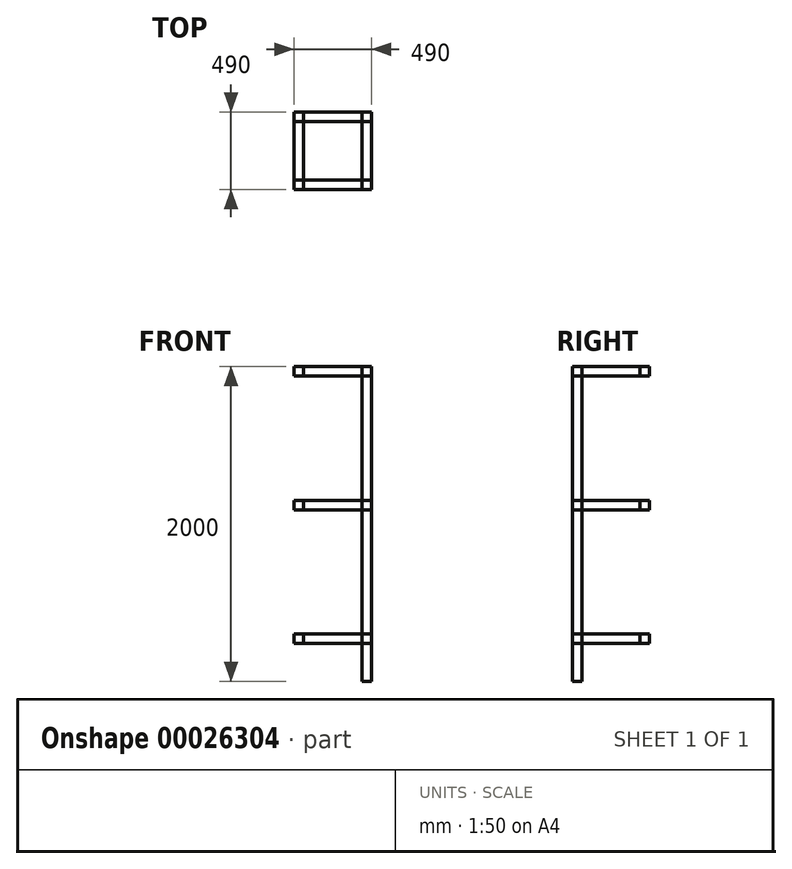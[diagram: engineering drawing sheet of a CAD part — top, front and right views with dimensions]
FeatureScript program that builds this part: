
annotation { "Feature Type Name" : "Feature", "Feature Type Description" : "" }
export const myFeature = defineFeature(function(context is Context, id is Id, definition is map)
    precondition{}
    {
        {
            var Q0;
            Q0=qCreatedBy(makeId("Top.planeOp"),FACE);
            var sketch = newSketch(context, id + "F0", { "sketchPlane" : qUnion([Q0])});
            skLineSegment(sketch, "E0.bottom", {"start": v(0, 0) * mm, "end": v(490, 0) * mm});
            skLineSegment(sketch, "E0.top", {"start": v(0, 490) * mm, "end": v(490, 490) * mm});
            skLineSegment(sketch, "E0.left", {"start": v(0, 0) * mm, "end": v(0, 490) * mm});
            skLineSegment(sketch, "E0.right", {"start": v(490, 0) * mm, "end": v(490, 490) * mm});
            skLineSegment(sketch, "E1.bottom", {"start": v(0, 0) * mm, "end": v(60, 0) * mm});
            skLineSegment(sketch, "E1.top", {"start": v(0, 60) * mm, "end": v(60, 60) * mm});
            skLineSegment(sketch, "E1.left", {"start": v(0, 0) * mm, "end": v(0, 60) * mm});
            skLineSegment(sketch, "E1.right", {"start": v(60, 0) * mm, "end": v(60, 60) * mm});
            skLineSegment(sketch, "E2.0.1.0", {"start": v(0, 490) * mm, "end": v(60, 490) * mm});
            skLineSegment(sketch, "E2.0.1.1", {"start": v(0, 430) * mm, "end": v(0, 490) * mm});
            skLineSegment(sketch, "E2.0.1.2", {"start": v(0, 430) * mm, "end": v(60, 430) * mm});
            skLineSegment(sketch, "E2.0.1.3", {"start": v(60, 430) * mm, "end": v(60, 490) * mm});
            skLineSegment(sketch, "E2.1.0.0", {"start": v(430, 60) * mm, "end": v(490, 60) * mm});
            skLineSegment(sketch, "E2.1.0.1", {"start": v(430, 0) * mm, "end": v(430, 60) * mm});
            skLineSegment(sketch, "E2.1.0.2", {"start": v(430, 0) * mm, "end": v(490, 0) * mm});
            skLineSegment(sketch, "E2.1.0.3", {"start": v(490, 0) * mm, "end": v(490, 60) * mm});
            skLineSegment(sketch, "E2.1.1.0", {"start": v(430, 490) * mm, "end": v(490, 490) * mm});
            skLineSegment(sketch, "E2.1.1.1", {"start": v(430, 430) * mm, "end": v(430, 490) * mm});
            skLineSegment(sketch, "E2.1.1.2", {"start": v(430, 430) * mm, "end": v(490, 430) * mm});
            skLineSegment(sketch, "E2.1.1.3", {"start": v(490, 430) * mm, "end": v(490, 490) * mm});
            skLineSegment(sketch, "E2.direction1", {"start": v(0, 60) * mm, "end": v(430, 60) * mm, "construction": true});
            skLineSegment(sketch, "E2.direction2", {"start": v(0, 60) * mm, "end": v(0, 490) * mm, "construction": true});
            skSolve(sketch);
        }
        {
            var Q0;
            Q0=qCreatedBy(makeId("Right.planeOp"),FACE);
            var sketch = newSketch(context, id + "F1", { "sketchPlane" : qUnion([Q0])});
            skLineSegment(sketch, "E3.bottom", {"start": v(0, 0) * mm, "end": v(60, 0) * mm});
            skLineSegment(sketch, "E3.top", {"start": v(0, -60) * mm, "end": v(60, -60) * mm});
            skLineSegment(sketch, "E3.left", {"start": v(0, 0) * mm, "end": v(0, -60) * mm});
            skLineSegment(sketch, "E3.right", {"start": v(60, 0) * mm, "end": v(60, -60) * mm});
            skLineSegment(sketch, "E4.0.1.0", {"start": v(0, -910) * mm, "end": v(60, -910) * mm});
            skLineSegment(sketch, "E4.0.1.1", {"start": v(0, -850) * mm, "end": v(60, -850) * mm});
            skLineSegment(sketch, "E4.0.1.2", {"start": v(60, -850) * mm, "end": v(60, -910) * mm});
            skLineSegment(sketch, "E4.0.1.3", {"start": v(0, -850) * mm, "end": v(0, -910) * mm});
            skLineSegment(sketch, "E4.0.2.0", {"start": v(0, -1760) * mm, "end": v(60, -1760) * mm});
            skLineSegment(sketch, "E4.0.2.1", {"start": v(0, -1700) * mm, "end": v(60, -1700) * mm});
            skLineSegment(sketch, "E4.0.2.2", {"start": v(60, -1700) * mm, "end": v(60, -1760) * mm});
            skLineSegment(sketch, "E4.0.2.3", {"start": v(0, -1700) * mm, "end": v(0, -1760) * mm});
            skLineSegment(sketch, "E4.1.0.0", {"start": v(430, -60) * mm, "end": v(490, -60) * mm});
            skLineSegment(sketch, "E4.1.0.1", {"start": v(430, 0) * mm, "end": v(490, 0) * mm});
            skLineSegment(sketch, "E4.1.0.2", {"start": v(490, 0) * mm, "end": v(490, -60) * mm});
            skLineSegment(sketch, "E4.1.0.3", {"start": v(430, 0) * mm, "end": v(430, -60) * mm});
            skLineSegment(sketch, "E4.1.1.0", {"start": v(430, -910) * mm, "end": v(490, -910) * mm});
            skLineSegment(sketch, "E4.1.1.1", {"start": v(430, -850) * mm, "end": v(490, -850) * mm});
            skLineSegment(sketch, "E4.1.1.2", {"start": v(490, -850) * mm, "end": v(490, -910) * mm});
            skLineSegment(sketch, "E4.1.1.3", {"start": v(430, -850) * mm, "end": v(430, -910) * mm});
            skLineSegment(sketch, "E4.1.2.0", {"start": v(430, -1760) * mm, "end": v(490, -1760) * mm});
            skLineSegment(sketch, "E4.1.2.1", {"start": v(430, -1700) * mm, "end": v(490, -1700) * mm});
            skLineSegment(sketch, "E4.1.2.2", {"start": v(490, -1700) * mm, "end": v(490, -1760) * mm});
            skLineSegment(sketch, "E4.1.2.3", {"start": v(430, -1700) * mm, "end": v(430, -1760) * mm});
            skLineSegment(sketch, "E4.direction1", {"start": v(0, -60) * mm, "end": v(430, -60) * mm, "construction": true});
            skLineSegment(sketch, "E4.direction2", {"start": v(0, -60) * mm, "end": v(0, -910) * mm, "construction": true});
            skSolve(sketch);
        }
        {
            var Q0;
            Q0=qCreatedBy(makeId("Front.planeOp"),FACE);
            var sketch = newSketch(context, id + "F2", { "sketchPlane" : qUnion([Q0])});
            skLineSegment(sketch, "E5.bottom", {"start": v(0, 0) * mm, "end": v(60, 0) * mm});
            skLineSegment(sketch, "E5.top", {"start": v(0, -60) * mm, "end": v(60, -60) * mm});
            skLineSegment(sketch, "E5.left", {"start": v(0, 0) * mm, "end": v(0, -60) * mm});
            skLineSegment(sketch, "E5.right", {"start": v(60, 0) * mm, "end": v(60, -60) * mm});
            skLineSegment(sketch, "E6.0.1.0", {"start": v(0, -850) * mm, "end": v(60, -850) * mm});
            skLineSegment(sketch, "E6.0.1.1", {"start": v(0, -850) * mm, "end": v(0, -910) * mm});
            skLineSegment(sketch, "E6.0.1.2", {"start": v(0, -910) * mm, "end": v(60, -910) * mm});
            skLineSegment(sketch, "E6.0.1.3", {"start": v(60, -850) * mm, "end": v(60, -910) * mm});
            skLineSegment(sketch, "E6.0.2.0", {"start": v(0, -1700) * mm, "end": v(60, -1700) * mm});
            skLineSegment(sketch, "E6.0.2.1", {"start": v(0, -1700) * mm, "end": v(0, -1760) * mm});
            skLineSegment(sketch, "E6.0.2.2", {"start": v(0, -1760) * mm, "end": v(60, -1760) * mm});
            skLineSegment(sketch, "E6.0.2.3", {"start": v(60, -1700) * mm, "end": v(60, -1760) * mm});
            skLineSegment(sketch, "E6.1.0.0", {"start": v(430, 0) * mm, "end": v(490, 0) * mm});
            skLineSegment(sketch, "E6.1.0.1", {"start": v(430, 0) * mm, "end": v(430, -60) * mm});
            skLineSegment(sketch, "E6.1.0.2", {"start": v(430, -60) * mm, "end": v(490, -60) * mm});
            skLineSegment(sketch, "E6.1.0.3", {"start": v(490, 0) * mm, "end": v(490, -60) * mm});
            skLineSegment(sketch, "E6.1.1.0", {"start": v(430, -850) * mm, "end": v(490, -850) * mm});
            skLineSegment(sketch, "E6.1.1.1", {"start": v(430, -850) * mm, "end": v(430, -910) * mm});
            skLineSegment(sketch, "E6.1.1.2", {"start": v(430, -910) * mm, "end": v(490, -910) * mm});
            skLineSegment(sketch, "E6.1.1.3", {"start": v(490, -850) * mm, "end": v(490, -910) * mm});
            skLineSegment(sketch, "E6.1.2.0", {"start": v(430, -1700) * mm, "end": v(490, -1700) * mm});
            skLineSegment(sketch, "E6.1.2.1", {"start": v(430, -1700) * mm, "end": v(430, -1760) * mm});
            skLineSegment(sketch, "E6.1.2.2", {"start": v(430, -1760) * mm, "end": v(490, -1760) * mm});
            skLineSegment(sketch, "E6.1.2.3", {"start": v(490, -1700) * mm, "end": v(490, -1760) * mm});
            skLineSegment(sketch, "E6.direction1", {"start": v(0, 0) * mm, "end": v(430, 0) * mm, "construction": true});
            skLineSegment(sketch, "E6.direction2", {"start": v(0, 0) * mm, "end": v(0, -850) * mm, "construction": true});
            skSolve(sketch);
        }
        {
            var Q0;
            Q0=makeQuery(id+"F0.imprint","IMPRINT",FACE,{"disambiguationData":[TD([[makeQuery(id+"F0.imprint","IMPRINT",EDGE,{"derivedFrom":sQuery(id+"F0.wireOp",EDGE,"E2.0.1.0")}),-1.0]])]});
            var Q1;
            Q1=makeQuery(id+"F0.imprint","IMPRINT",FACE,{"disambiguationData":[TD([[makeQuery(id+"F0.imprint","IMPRINT",EDGE,{"derivedFrom":sQuery(id+"F0.wireOp",EDGE,"E2.1.1.0")}),-1.0]])]});
            var Q2;
            Q2=makeQuery(id+"F0.imprint","IMPRINT",FACE,{"disambiguationData":[TD([[makeQuery(id+"F0.imprint","IMPRINT",EDGE,{"derivedFrom":sQuery(id+"F0.wireOp",EDGE,"E2.1.0.0")}),-1.0]])]});
            var Q3;
            Q3=makeQuery(id+"F0.imprint","IMPRINT",FACE,{"disambiguationData":[TD([[makeQuery(id+"F0.imprint","IMPRINT",EDGE,{"derivedFrom":sQuery(id+"F0.wireOp",EDGE,"E1.bottom")}),1.0]])]});
            extrude(context, id + "F3", {"entities" : qUnion([Q0, Q1, Q2, Q3]), "oppositeDirection" : true, "depth" : 2000 * mm});
        }
        {
            var Q0;
            Q0=makeQuery(id+"F1.imprint","IMPRINT",FACE,{"disambiguationData":[TD([[makeQuery(id+"F1.imprint","IMPRINT",EDGE,{"derivedFrom":sQuery(id+"F1.wireOp",EDGE,"E4.1.0.0")}),1.0]])]});
            var Q1;
            Q1=makeQuery(id+"F1.imprint","IMPRINT",FACE,{"disambiguationData":[TD([[makeQuery(id+"F1.imprint","IMPRINT",EDGE,{"derivedFrom":sQuery(id+"F1.wireOp",EDGE,"E4.1.1.0")}),1.0]])]});
            var Q2;
            Q2=makeQuery(id+"F1.imprint","IMPRINT",FACE,{"disambiguationData":[TD([[makeQuery(id+"F1.imprint","IMPRINT",EDGE,{"derivedFrom":sQuery(id+"F1.wireOp",EDGE,"E4.1.2.0")}),1.0]])]});
            var Q3;
            Q3=makeQuery(id+"F1.imprint","IMPRINT",FACE,{"disambiguationData":[TD([[makeQuery(id+"F1.imprint","IMPRINT",EDGE,{"derivedFrom":sQuery(id+"F1.wireOp",EDGE,"E4.0.1.0")}),1.0]])]});
            var Q4;
            Q4=makeQuery(id+"F1.imprint","IMPRINT",FACE,{"disambiguationData":[TD([[makeQuery(id+"F1.imprint","IMPRINT",EDGE,{"derivedFrom":sQuery(id+"F1.wireOp",EDGE,"E4.0.2.0")}),1.0]])]});
            var Q5;
            Q5=makeQuery(id+"F1.imprint","IMPRINT",FACE,{"disambiguationData":[TD([[makeQuery(id+"F1.imprint","IMPRINT",EDGE,{"derivedFrom":sQuery(id+"F1.wireOp",EDGE,"E3.bottom")}),-1.0]])]});
            extrude(context, id + "F4", {"entities" : qUnion([Q0, Q1, Q2, Q3, Q4, Q5]), "depth" : 490 * mm});
        }
        {
            var Q0;
            Q0=makeQuery(id+"F2.imprint","IMPRINT",FACE,{"disambiguationData":[TD([[makeQuery(id+"F2.imprint","IMPRINT",EDGE,{"derivedFrom":sQuery(id+"F2.wireOp",EDGE,"E6.1.0.0")}),-1.0]])]});
            var Q1;
            Q1=makeQuery(id+"F2.imprint","IMPRINT",FACE,{"disambiguationData":[TD([[makeQuery(id+"F2.imprint","IMPRINT",EDGE,{"derivedFrom":sQuery(id+"F2.wireOp",EDGE,"E5.bottom")}),-1.0]])]});
            var Q2;
            Q2=makeQuery(id+"F2.imprint","IMPRINT",FACE,{"disambiguationData":[TD([[makeQuery(id+"F2.imprint","IMPRINT",EDGE,{"derivedFrom":sQuery(id+"F2.wireOp",EDGE,"E6.0.1.0")}),-1.0]])]});
            var Q3;
            Q3=makeQuery(id+"F2.imprint","IMPRINT",FACE,{"disambiguationData":[TD([[makeQuery(id+"F2.imprint","IMPRINT",EDGE,{"derivedFrom":sQuery(id+"F2.wireOp",EDGE,"E6.1.1.0")}),-1.0]])]});
            var Q4;
            Q4=makeQuery(id+"F2.imprint","IMPRINT",FACE,{"disambiguationData":[TD([[makeQuery(id+"F2.imprint","IMPRINT",EDGE,{"derivedFrom":sQuery(id+"F2.wireOp",EDGE,"E6.0.2.0")}),-1.0]])]});
            var Q5;
            Q5=makeQuery(id+"F2.imprint","IMPRINT",FACE,{"disambiguationData":[TD([[makeQuery(id+"F2.imprint","IMPRINT",EDGE,{"derivedFrom":sQuery(id+"F2.wireOp",EDGE,"E6.1.2.0")}),-1.0]])]});
            extrude(context, id + "F5", {"entities" : qUnion([Q0, Q1, Q2, Q3, Q4, Q5]), "oppositeDirection" : true, "depth" : 490 * mm});
        }
    });
